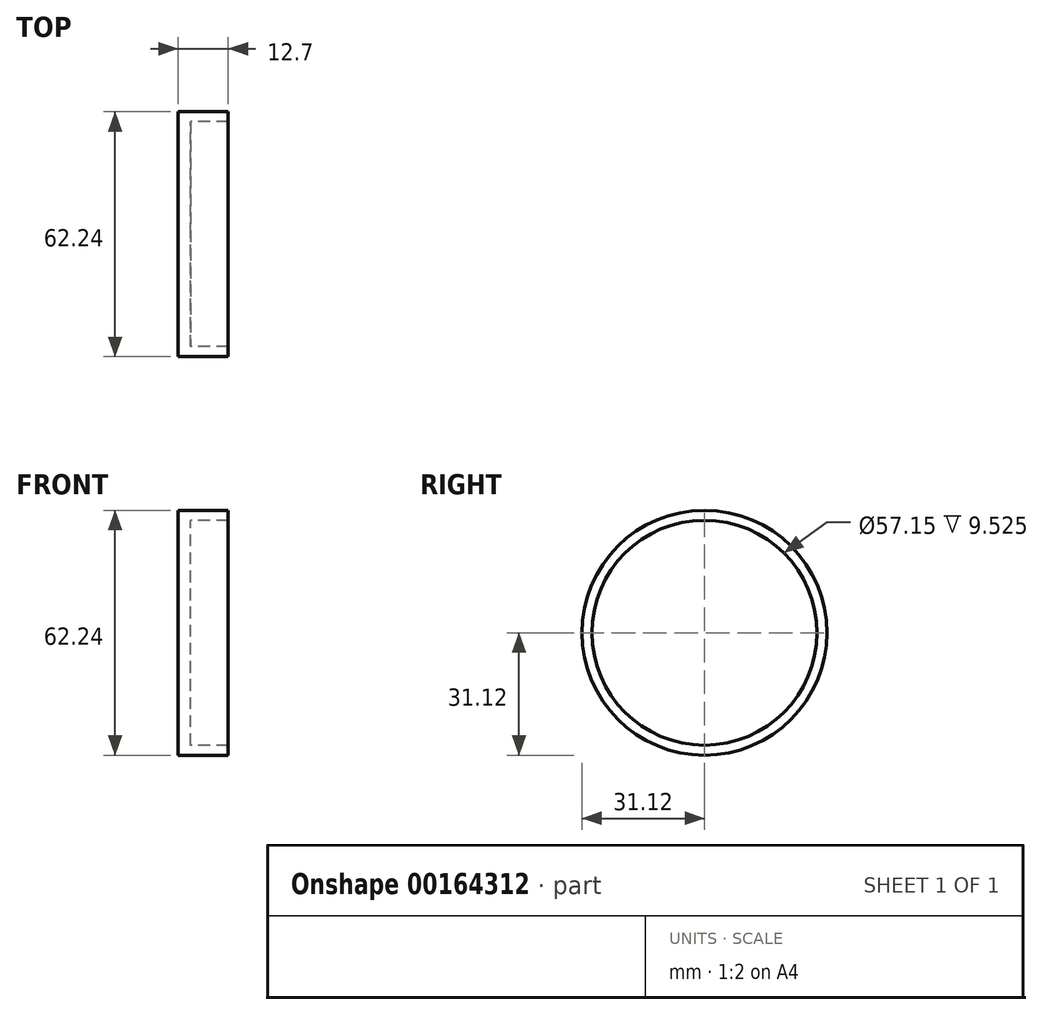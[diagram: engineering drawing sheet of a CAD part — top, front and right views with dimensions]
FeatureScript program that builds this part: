
annotation { "Feature Type Name" : "Feature", "Feature Type Description" : "" }
export const myFeature = defineFeature(function(context is Context, id is Id, definition is map)
    precondition{}
    {
        {
            var Q0;
            Q0=qCreatedBy(makeId("Right.planeOp"),FACE);
            var sketch = newSketch(context, id + "F0", { "sketchPlane" : qUnion([Q0])});
            skCircle(sketch, "E0", {"center": v(0, 0) * mm, "radius": 31.12 * mm});
            skCircle(sketch, "E1", {"center": v(0, 0) * mm, "radius": 28.58 * mm});
            skSolve(sketch);
        }
        {
            var Q0;
            Q0 = qSketchRegion(id + "F0", true);
            var Q1;
            Q1=makeQuery(id+"F0.imprint","IMPRINT",FACE,{"disambiguationData":[TD([[makeQuery(id+"F0.imprint","IMPRINT",EDGE,{"derivedFrom":sQuery(id+"F0.wireOp",EDGE,"E1")}),1.0]])]});
            extrude(context, id + "F1", {"entities" : qUnion([Q0, Q1]), "depth" : 3.17 * mm});
        }
        {
            var Q0;
            Q0=makeQuery(id+"F0.imprint","IMPRINT",FACE,{"disambiguationData":[TD([[makeQuery(id+"F0.imprint","IMPRINT",EDGE,{"derivedFrom":sQuery(id+"F0.wireOp",EDGE,"E0")}),1.0]])]});
            extrude(context, id + "F2", {"entities" : qUnion([Q0]), "operationType" : NewBodyOperationType.ADD, "depth" : 12.7 * mm});
        }
    });
